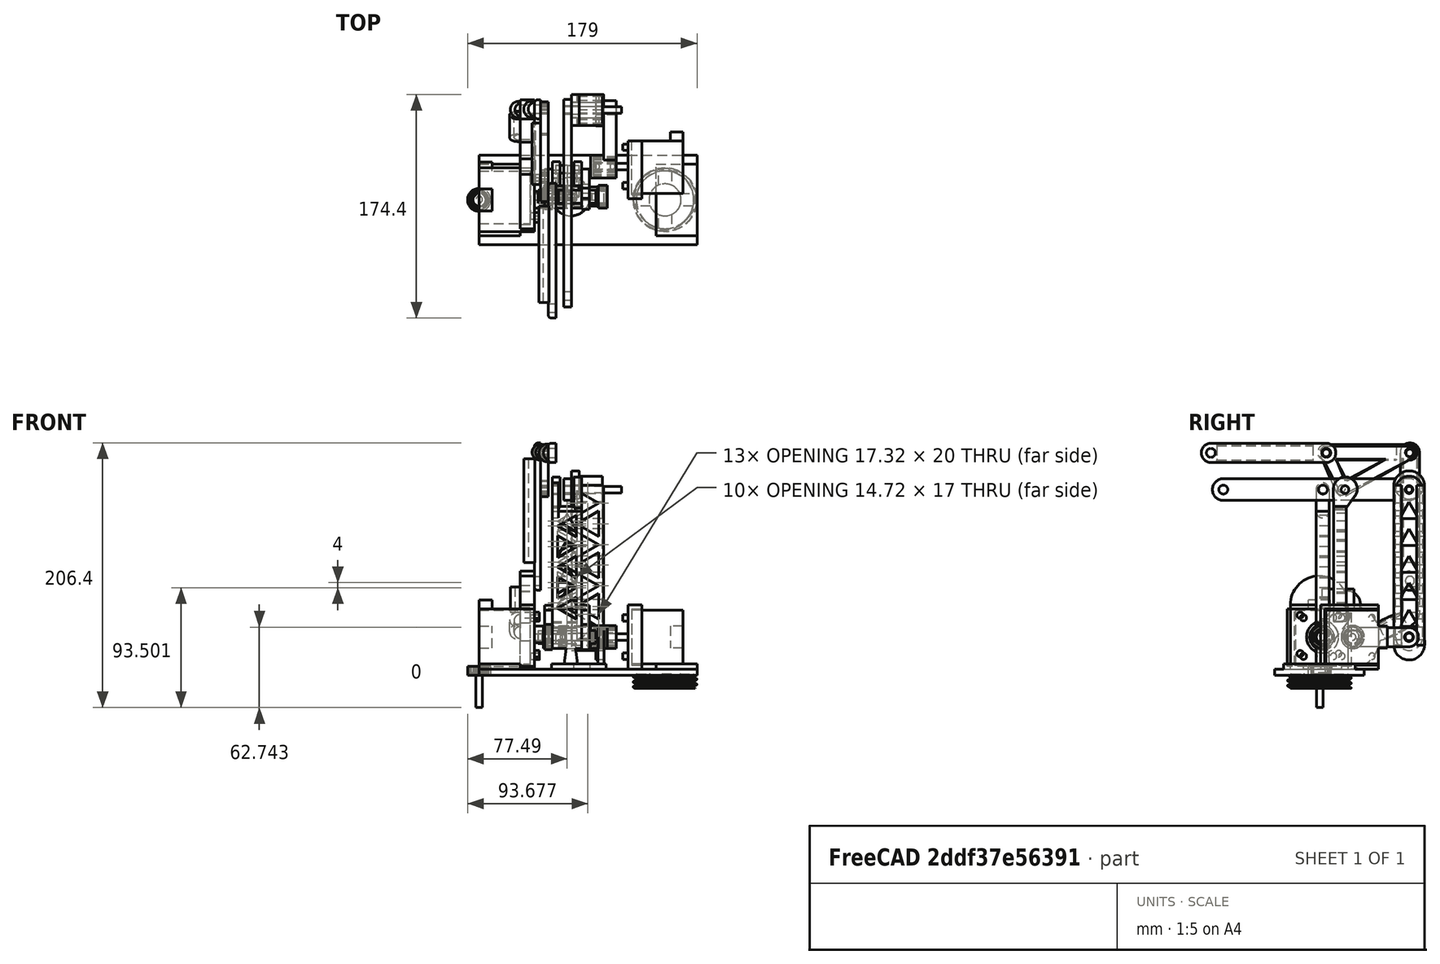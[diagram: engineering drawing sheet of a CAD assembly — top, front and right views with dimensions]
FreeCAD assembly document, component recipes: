
FREECAD ASSEMBLY — COMPONENT RECIPES ("my_arm")

This assembly document has 27 components, labeled P0..P26 below (a component is one placed body or linked part). 4 of them carry a construction recipe — the FreeCAD feature program that regenerates the part from scratch, quoted from this document or its linked companion documents; the rest are supplied as boundary geometry only. No exploded tour is included for this assembly.
COMPONENT P0 — recipe-attached ("Body", modeled in this document).
Construction recipe (the document's own serialized feature program — sketch geometry with constraints, then the solid features built on it; lengths are millimeters unless a unit is written):

FEATURE [PartDesign::FeatureBase] BaseFeature
  BaseFeature = -> Fusion034
FEATURE [Sketcher::SketchObject] Sketch030
  FullyConstrained = false
  MapMode = 5
  Support = -> [XY_Plane]
  sketch-geometry (8):
    g0: Circle CenterX=0 CenterY=0 CenterZ=0 NormalX=0 NormalY=0 NormalZ=1 AngleXU=0 Radius=4.9
    g1: Circle CenterX=0 CenterY=0 CenterZ=0 NormalX=0 NormalY=0 NormalZ=1 AngleXU=0 Radius=6.4
    g2: Circle CenterX=0 CenterY=0 CenterZ=0 NormalX=0 NormalY=0 NormalZ=1 AngleXU=0 Radius=7.5
    g3: Circle CenterX=0 CenterY=0 CenterZ=0 NormalX=0 NormalY=0 NormalZ=1 AngleXU=0 Radius=9
    g4: LineSegment StartX=-2 StartY=0 StartZ=0 EndX=2 EndY=0 EndZ=0
    g5: LineSegment StartX=2 StartY=0 StartZ=0 EndX=2 EndY=10.9979 EndZ=0
    g6: LineSegment StartX=2 StartY=10.9979 StartZ=0 EndX=-2 EndY=10.9979 EndZ=0
    g7: LineSegment StartX=-2 StartY=10.9979 StartZ=0 EndX=-2 EndY=0 EndZ=0
  constraints (18):
    c: Coincident(g0,g-1)
    c: Coincident(g1,g0)
    c: Coincident(g2,g0)
    c: Coincident(g3,g0)
    c: Radius(g0) = 4.9
    c: Radius(g1) = 6.4
    c: Radius(g2) = 7.5
    c: Radius(g3) = 9
    c: Coincident(g4,g5)
    c: Coincident(g5,g6)
    c: Coincident(g6,g7)
    c: Coincident(g7,g4)
    c: Horizontal(g6)
    c: Vertical(g5)
    c: Vertical(g7)
    c: PointOnObject(g4,g-1)
    c: Symmetric(g4,g4,g-2)
    c: DistanceX(g6,g6) = 4
FEATURE [PartDesign::Pad] Pad
  BaseFeature = -> BaseFeature
  Direction = (1,1,1)
  Length = 2
  Length2 = 100
  Profile = -> BaseFeature [Face14,Face19,Face16,Face21,Face20]
  Type = 0
FEATURE [PartDesign::Body] Body
  BaseFeature = -> Fusion034
  Group = -> [BaseFeature,Sketch030,Pad]
  Origin = -> Origin
  Tip = -> Pad
COMPONENT P1 — recipe-attached ("Body001", modeled in this document).
Construction recipe (the document's own serialized feature program — sketch geometry with constraints, then the solid features built on it; lengths are millimeters unless a unit is written):

FEATURE [PartDesign::FeatureBase] BaseFeature001
  BaseFeature = -> Cut019
FEATURE [PartDesign::Fillet] Fillet003  label="Fillet"
  Base = -> BaseFeature001 [Edge103]
  BaseFeature = -> BaseFeature001
  Radius = 0.5
  SupportTransform = false
FEATURE [PartDesign::Body] Body001
  BaseFeature = -> Cut019
  Group = -> [BaseFeature001,Fillet003]
  Origin = -> Origin001
  Tip = -> Fillet003
COMPONENT P2 — recipe-attached ("Body002", modeled in this document).
Construction recipe (the document's own serialized feature program — sketch geometry with constraints, then the solid features built on it; lengths are millimeters unless a unit is written):

FEATURE [Sketcher::SketchObject] Sketch040
  FullyConstrained = false
  MapMode = 5
  Support = -> [XY_Plane002]
  sketch-geometry (8):
    g0: Circle CenterX=0 CenterY=0 CenterZ=0 NormalX=0 NormalY=0 NormalZ=1 AngleXU=0 Radius=4.9
    g1: Circle CenterX=0 CenterY=0 CenterZ=0 NormalX=0 NormalY=0 NormalZ=1 AngleXU=0 Radius=6.4
    g2: Circle CenterX=0 CenterY=0 CenterZ=0 NormalX=0 NormalY=0 NormalZ=1 AngleXU=0 Radius=7.5
    g3: Circle CenterX=0 CenterY=0 CenterZ=0 NormalX=0 NormalY=0 NormalZ=1 AngleXU=0 Radius=9
    g4: LineSegment StartX=-2 StartY=0 StartZ=0 EndX=2 EndY=0 EndZ=0
    g5: LineSegment StartX=2 StartY=0 StartZ=0 EndX=2 EndY=10.9979 EndZ=0
    g6: LineSegment StartX=2 StartY=10.9979 StartZ=0 EndX=-2 EndY=10.9979 EndZ=0
    g7: LineSegment StartX=-2 StartY=10.9979 StartZ=0 EndX=-2 EndY=0 EndZ=0
  constraints (18):
    c: Coincident(g0,g-1)
    c: Coincident(g1,g0)
    c: Coincident(g2,g0)
    c: Coincident(g3,g0)
    c: Radius(g0) = 4.9
    c: Radius(g1) = 6.4
    c: Radius(g2) = 7.5
    c: Radius(g3) = 9
    c: Coincident(g4,g5)
    c: Coincident(g5,g6)
    c: Coincident(g6,g7)
    c: Coincident(g7,g4)
    c: Horizontal(g6)
    c: Vertical(g5)
    c: Vertical(g7)
    c: PointOnObject(g4,g-1)
    c: Symmetric(g4,g4,g-2)
    c: DistanceX(g6,g6) = 4
FEATURE [PartDesign::FeatureBase] BaseFeature005
  BaseFeature = -> Fusion049
FEATURE [PartDesign::Pad] Pad003
  BaseFeature = -> BaseFeature005
  Direction = (1,1,1)
  Length = 2
  Length2 = 100
  Profile = -> BaseFeature005 [Face14,Face19,Face16,Face21,Face20]
  Type = 0
FEATURE [PartDesign::Body] Body002
  BaseFeature = -> Fusion049
  Group = -> [BaseFeature005,Sketch040,Pad003]
  Origin = -> Origin002
  Tip = -> Pad003
COMPONENT P3 — recipe-attached ("Body003", modeled in this document).
Construction recipe (the document's own serialized feature program — sketch geometry with constraints, then the solid features built on it; lengths are millimeters unless a unit is written):

FEATURE [PartDesign::FeatureBase] BaseFeature006
  BaseFeature = -> Cut032
FEATURE [PartDesign::Fillet] Fillet004
  Base = -> BaseFeature006 [Edge103]
  BaseFeature = -> BaseFeature006
  Radius = 0.5
  SupportTransform = false
FEATURE [PartDesign::Body] Body003
  BaseFeature = -> Cut032
  Group = -> [BaseFeature006,Fillet004]
  Origin = -> Origin003
  Tip = -> Fillet004
COMPONENT P4 — geometry summary ("tonillo motor001"; no construction recipe available for this part):
  bounding box: 5.0 x 5.0 x 4.0 mm
  tessellated surface: 500 triangles
  volume: 79 mm^3 (79% of its bounding box)
  symmetry: 2-fold rotationally symmetric about the x axis; 2-fold rotationally symmetric about the y axis; revolution-symmetric about the z axis through its bounding-box center; mirror-symmetric across its x mid-plane, y mid-plane, z mid-plane
COMPONENT P5 — geometry summary ("tonillo motor002"; no construction recipe available for this part):
  bounding box: 5.0 x 5.0 x 4.0 mm
  tessellated surface: 500 triangles
  volume: 79 mm^3 (79% of its bounding box)
  symmetry: 2-fold rotationally symmetric about the x axis; 2-fold rotationally symmetric about the y axis; revolution-symmetric about the z axis through its bounding-box center; mirror-symmetric across its x mid-plane, y mid-plane, z mid-plane
COMPONENT P6 — geometry summary ("tonillo motor003"; no construction recipe available for this part):
  bounding box: 5.0 x 5.0 x 4.0 mm
  tessellated surface: 500 triangles
  volume: 79 mm^3 (79% of its bounding box)
  symmetry: 2-fold rotationally symmetric about the x axis; 2-fold rotationally symmetric about the y axis; revolution-symmetric about the z axis through its bounding-box center; mirror-symmetric across its x mid-plane, y mid-plane, z mid-plane
COMPONENT P7 — geometry summary ("tonillo motor005"; no construction recipe available for this part):
  bounding box: 5.0 x 5.0 x 4.0 mm
  tessellated surface: 500 triangles
  volume: 79 mm^3 (79% of its bounding box)
  symmetry: 2-fold rotationally symmetric about the x axis; 2-fold rotationally symmetric about the y axis; revolution-symmetric about the z axis through its bounding-box center; mirror-symmetric across its x mid-plane, y mid-plane, z mid-plane
COMPONENT P8 — geometry summary ("tonillo motor006"; no construction recipe available for this part):
  bounding box: 5.0 x 5.0 x 4.0 mm
  tessellated surface: 500 triangles
  volume: 79 mm^3 (79% of its bounding box)
  symmetry: 2-fold rotationally symmetric about the x axis; 2-fold rotationally symmetric about the y axis; revolution-symmetric about the z axis through its bounding-box center; mirror-symmetric across its x mid-plane, y mid-plane, z mid-plane
COMPONENT P9 — geometry summary ("tonillo motor007"; no construction recipe available for this part):
  bounding box: 5.0 x 5.0 x 4.0 mm
  tessellated surface: 500 triangles
  volume: 79 mm^3 (79% of its bounding box)
  symmetry: 2-fold rotationally symmetric about the x axis; 2-fold rotationally symmetric about the y axis; revolution-symmetric about the z axis through its bounding-box center; mirror-symmetric across its x mid-plane, y mid-plane, z mid-plane
COMPONENT P10 — geometry summary ("lateral der"; no construction recipe available for this part):
  bounding box: 45.0 x 8.0 x 3.0 mm
  tessellated surface: 12 triangles
  volume: 1080 mm^3 (100% of its bounding box)
  symmetry: 2-fold rotationally symmetric about the x axis; 2-fold rotationally symmetric about the y axis; 2-fold rotationally symmetric about the z axis; mirror-symmetric across its x mid-plane, y mid-plane, z mid-plane
COMPONENT P11 — geometry summary ("tonillo motor008"; no construction recipe available for this part):
  bounding box: 5.0 x 5.0 x 4.0 mm
  tessellated surface: 500 triangles
  volume: 79 mm^3 (79% of its bounding box)
  symmetry: 2-fold rotationally symmetric about the x axis; 2-fold rotationally symmetric about the y axis; revolution-symmetric about the z axis through its bounding-box center; mirror-symmetric across its x mid-plane, y mid-plane, z mid-plane
COMPONENT P12 — geometry summary ("lateral der001"; no construction recipe available for this part):
  bounding box: 45.0 x 8.0 x 3.0 mm
  tessellated surface: 12 triangles
  volume: 1080 mm^3 (100% of its bounding box)
  symmetry: 2-fold rotationally symmetric about the x axis; 2-fold rotationally symmetric about the y axis; 2-fold rotationally symmetric about the z axis; mirror-symmetric across its x mid-plane, y mid-plane, z mid-plane
COMPONENT P13 — geometry summary ("tonillo motor010"; no construction recipe available for this part):
  bounding box: 5.0 x 5.0 x 4.0 mm
  tessellated surface: 500 triangles
  volume: 79 mm^3 (79% of its bounding box)
  symmetry: 2-fold rotationally symmetric about the x axis; 2-fold rotationally symmetric about the y axis; revolution-symmetric about the z axis through its bounding-box center; mirror-symmetric across its x mid-plane, y mid-plane, z mid-plane
COMPONENT P14 — geometry summary ("tonillo motor011"; no construction recipe available for this part):
  bounding box: 5.0 x 5.0 x 4.0 mm
  tessellated surface: 500 triangles
  volume: 79 mm^3 (79% of its bounding box)
  symmetry: 2-fold rotationally symmetric about the x axis; 2-fold rotationally symmetric about the y axis; revolution-symmetric about the z axis through its bounding-box center; mirror-symmetric across its x mid-plane, y mid-plane, z mid-plane
COMPONENT P15 — geometry summary ("soporte motor001"; no construction recipe available for this part):
  bounding box: 56.0 x 32.0 x 4.0 mm
  tessellated surface: 12 triangles
  volume: 7168 mm^3 (100% of its bounding box)
  symmetry: 2-fold rotationally symmetric about the x axis; 2-fold rotationally symmetric about the y axis; 2-fold rotationally symmetric about the z axis; mirror-symmetric across its x mid-plane, y mid-plane, z mid-plane
COMPONENT P16 — geometry summary ("tonillo motor012"; no construction recipe available for this part):
  bounding box: 8.0 x 5.0 x 5.0 mm
  tessellated surface: 500 triangles
  volume: 157 mm^3 (79% of its bounding box)
  symmetry: 2-fold rotationally symmetric about the x axis; 2-fold rotationally symmetric about the y axis; revolution-symmetric about the z axis through its bounding-box center; mirror-symmetric across its x mid-plane, y mid-plane, z mid-plane
COMPONENT P17 — geometry summary ("lateral der002"; no construction recipe available for this part):
  bounding box: 45.0 x 8.0 x 3.0 mm
  tessellated surface: 12 triangles
  volume: 1080 mm^3 (100% of its bounding box)
  symmetry: 2-fold rotationally symmetric about the x axis; 2-fold rotationally symmetric about the y axis; 2-fold rotationally symmetric about the z axis; mirror-symmetric across its x mid-plane, y mid-plane, z mid-plane
COMPONENT P18 — geometry summary ("tonillo motor014"; no construction recipe available for this part):
  bounding box: 8.0 x 5.0 x 5.0 mm
  tessellated surface: 500 triangles
  volume: 157 mm^3 (79% of its bounding box)
  symmetry: 2-fold rotationally symmetric about the x axis; 2-fold rotationally symmetric about the y axis; revolution-symmetric about the z axis through its bounding-box center; mirror-symmetric across its x mid-plane, y mid-plane, z mid-plane
COMPONENT P19 — geometry summary ("tonillo motor015"; no construction recipe available for this part):
  bounding box: 8.0 x 5.0 x 5.0 mm
  tessellated surface: 500 triangles
  volume: 157 mm^3 (79% of its bounding box)
  symmetry: 2-fold rotationally symmetric about the x axis; 2-fold rotationally symmetric about the y axis; revolution-symmetric about the z axis through its bounding-box center; mirror-symmetric across its x mid-plane, y mid-plane, z mid-plane
COMPONENT P20 — geometry summary ("Union motor centro001"; no construction recipe available for this part):
  bounding box: 34.8 x 31.4 x 6.0 mm
  tessellated surface: 1,140 triangles
  volume: 3522 mm^3 (54% of its bounding box)
  symmetry: mirror-symmetric across its x mid-plane
COMPONENT P21 — geometry summary ("Union brazo central001"; no construction recipe available for this part):
  bounding box: 25.6 x 18.6 x 6.0 mm
  tessellated surface: 820 triangles
  volume: 2073 mm^3 (73% of its bounding box)
  symmetry: mirror-symmetric across its x mid-plane
COMPONENT P22 — geometry summary ("Union brazo central003"; no construction recipe available for this part):
  bounding box: 25.6 x 18.6 x 6.0 mm
  tessellated surface: 820 triangles
  volume: 2073 mm^3 (73% of its bounding box)
  symmetry: mirror-symmetric across its x mid-plane
COMPONENT P23 — geometry summary ("Palo triangular001"; no construction recipe available for this part):
  bounding box: 125.0 x 25.0 x 6.0 mm
  tessellated surface: 124 triangles
  volume: 11475 mm^3 (61% of its bounding box)
  symmetry: 2-fold rotationally symmetric about the x axis; mirror-symmetric across its y mid-plane, z mid-plane
COMPONENT P24 — geometry summary ("Union motor centro003"; no construction recipe available for this part):
  bounding box: 34.8 x 31.4 x 6.0 mm
  tessellated surface: 1,140 triangles
  volume: 3522 mm^3 (54% of its bounding box)
  symmetry: mirror-symmetric across its x mid-plane
COMPONENT P25 — geometry summary ("Union brazo central005"; no construction recipe available for this part):
  bounding box: 24.2 x 18.6 x 6.0 mm
  tessellated surface: 820 triangles
  volume: 1942 mm^3 (72% of its bounding box)
  symmetry: mirror-symmetric across its x mid-plane
COMPONENT P26 — geometry summary ("union centro_arriba001"; no construction recipe available for this part):
  bounding box: 27.3 x 10.0 x 5.0 mm
  tessellated surface: 1,016 triangles
  volume: 1066 mm^3 (78% of its bounding box)
  symmetry: mirror-symmetric across its x mid-plane
PROVENANCE & LICENSES
A FreeCAD (.FCStd) document from a public repository crawl; recipes are the document's own serialized feature recipes (and, for linked parts, companion documents' recipes).
License: lgpl-2.1.
